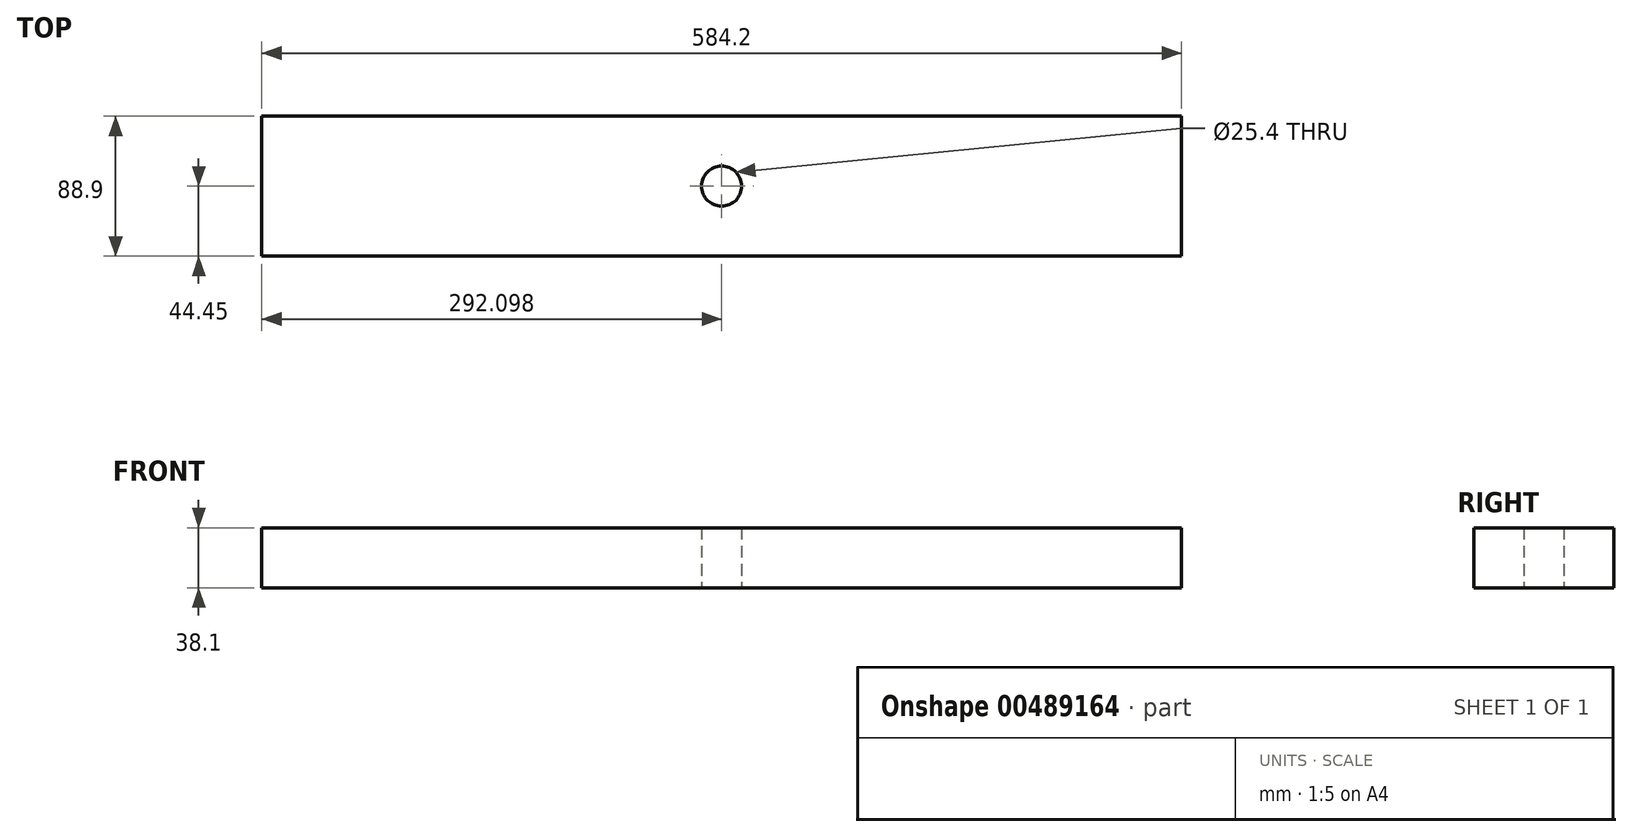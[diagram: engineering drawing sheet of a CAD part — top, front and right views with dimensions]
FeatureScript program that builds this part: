
annotation { "Feature Type Name" : "Feature", "Feature Type Description" : "" }
export const myFeature = defineFeature(function(context is Context, id is Id, definition is map)
    precondition{}
    {
        {
            var Q0;
            Q0=qCreatedBy(makeId("Top.planeOp"),FACE);
            var sketch = newSketch(context, id + "F0", { "sketchPlane" : qUnion([Q0])});
            skLineSegment(sketch, "E0.bottom", {"start": v(-291.12, 82.23) * mm, "end": v(293.08, 82.23) * mm});
            skLineSegment(sketch, "E0.top", {"start": v(-291.12, -6.67) * mm, "end": v(293.08, -6.67) * mm});
            skLineSegment(sketch, "E0.left", {"start": v(-291.12, 82.23) * mm, "end": v(-291.12, -6.67) * mm});
            skLineSegment(sketch, "E0.right", {"start": v(293.08, 82.23) * mm, "end": v(293.08, -6.67) * mm});
            skCircle(sketch, "E1", {"center": v(0.98, 37.78) * mm, "radius": 12.7 * mm});
            skSolve(sketch);
        }
        {
            var Q0;
            Q0=makeQuery(id+"F0.imprint","IMPRINT",FACE,{"disambiguationData":[TD([[makeQuery(id+"F0.imprint","IMPRINT",EDGE,{"derivedFrom":sQuery(id+"F0.wireOp",EDGE,"E0.bottom")}),-1.0]])]});
            extrude(context, id + "F1", {"entities" : qUnion([Q0]), "depth" : 38.1 * mm, "offsetDistance" : 25.4 * mm, "symmetric" : true});
        }
    });
